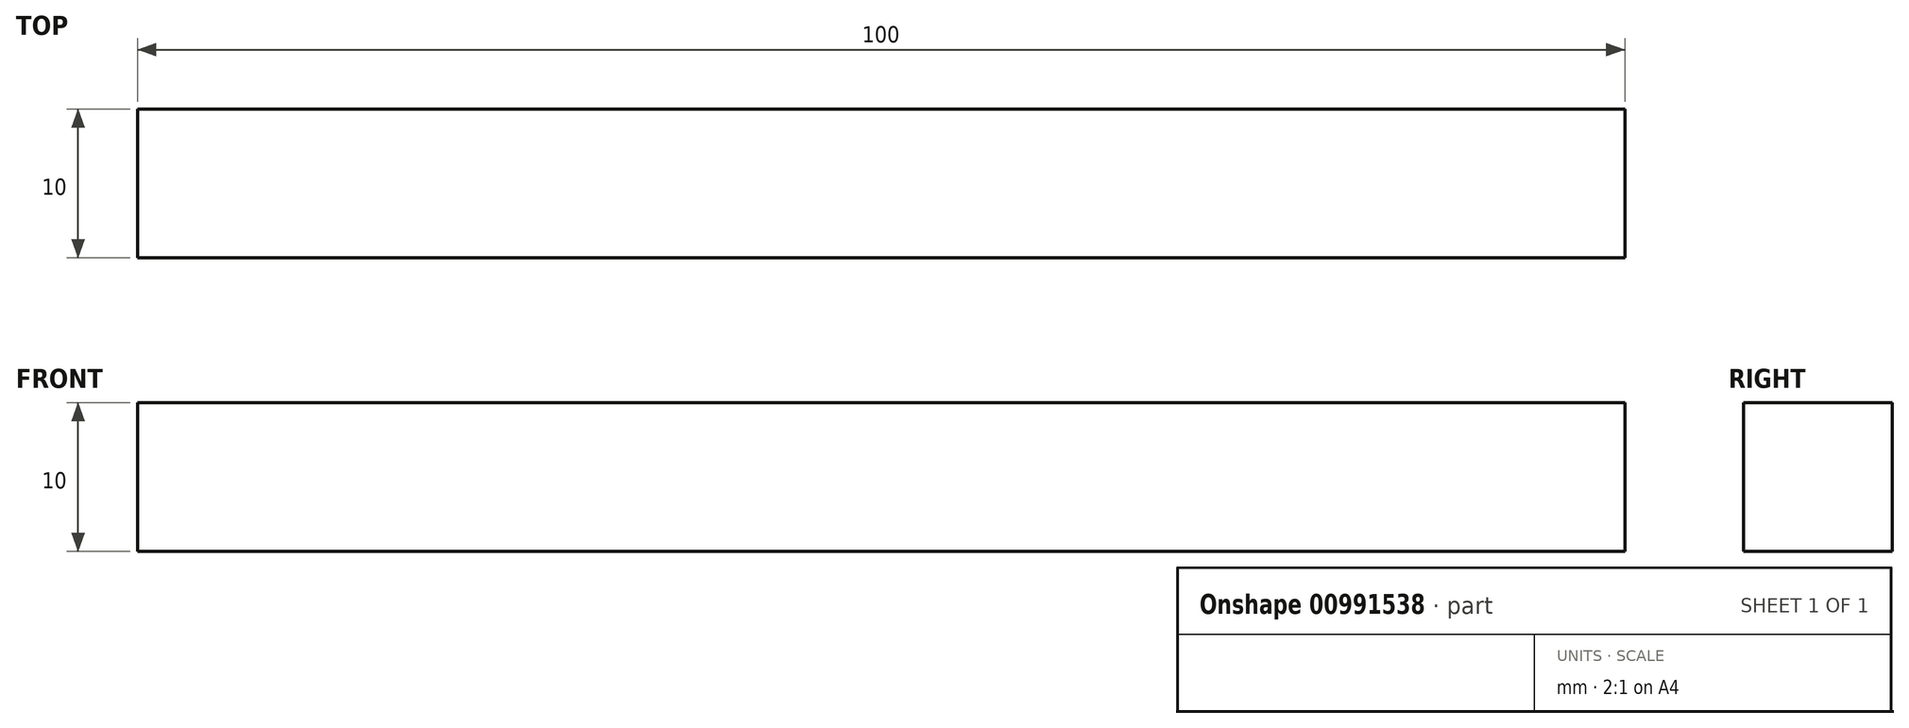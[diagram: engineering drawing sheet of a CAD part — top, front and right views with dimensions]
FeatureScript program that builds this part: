
annotation { "Feature Type Name" : "Feature", "Feature Type Description" : "" }
export const myFeature = defineFeature(function(context is Context, id is Id, definition is map)
    precondition{}
    {
        {
            var Q0;
            Q0=qCreatedBy(makeId("Top.planeOp"),FACE);
            var sketch = newSketch(context, id + "F0", { "sketchPlane" : qUnion([Q0])});
            skLineSegment(sketch, "E0.bottom", {"start": v(0, 0) * mm, "end": v(100, 0) * mm});
            skLineSegment(sketch, "E0.top", {"start": v(0, -10) * mm, "end": v(100, -10) * mm});
            skLineSegment(sketch, "E0.left", {"start": v(0, 0) * mm, "end": v(0, -10) * mm});
            skLineSegment(sketch, "E0.right", {"start": v(100, 0) * mm, "end": v(100, -10) * mm});
            skSolve(sketch);
        }
        {
            var Q0;
            Q0 = qSketchRegion(id + "F0", true);
            extrude(context, id + "F1", {"entities" : qUnion([Q0]), "depth" : 10 * mm, "offsetDistance" : 25 * mm});
        }
    });
